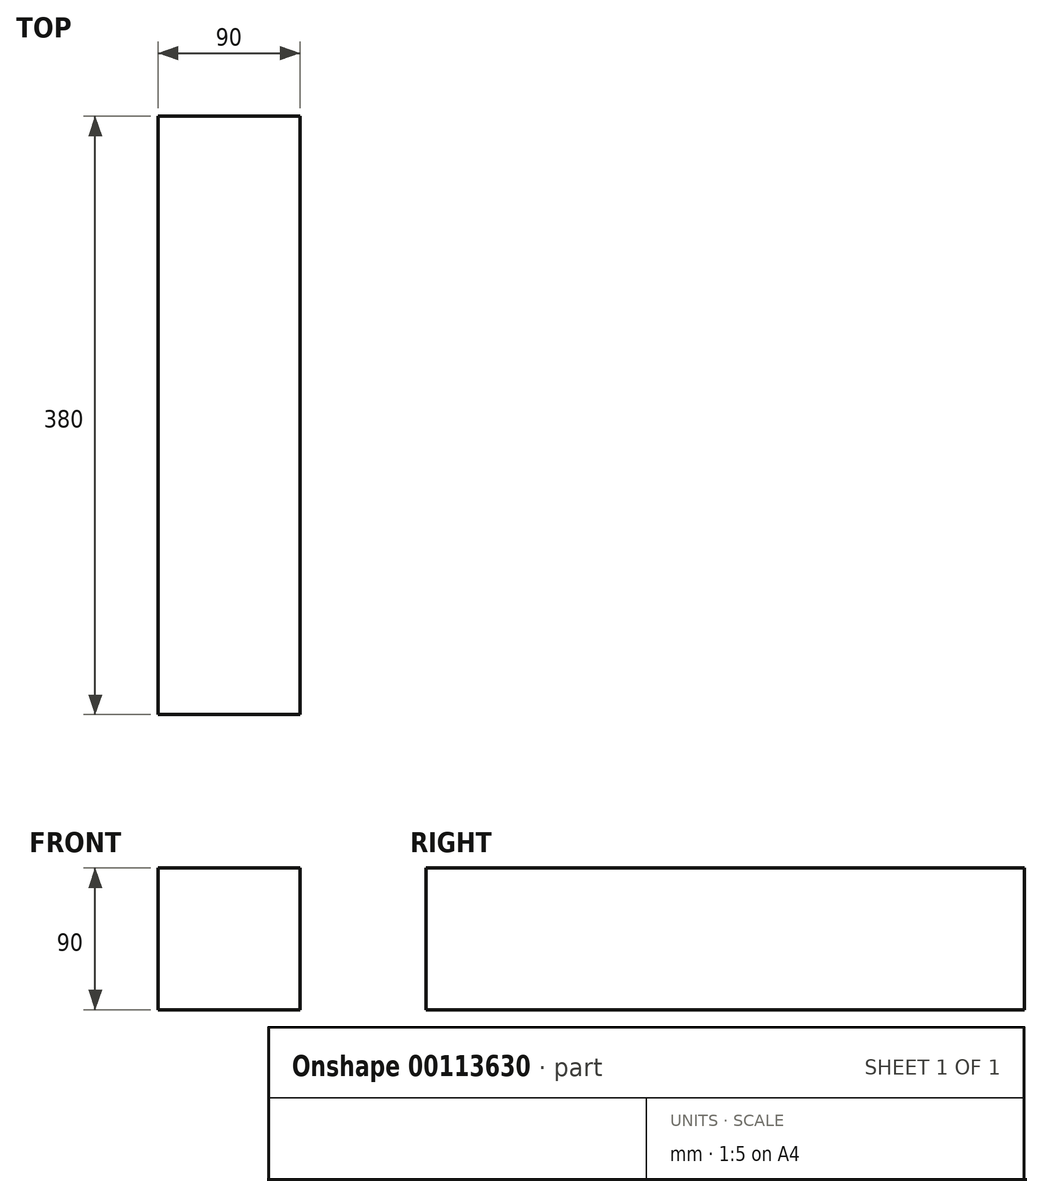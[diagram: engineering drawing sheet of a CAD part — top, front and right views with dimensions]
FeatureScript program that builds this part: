
annotation { "Feature Type Name" : "Feature", "Feature Type Description" : "" }
export const myFeature = defineFeature(function(context is Context, id is Id, definition is map)
    precondition{}
    {
        {
            var Q0;
            Q0=qCreatedBy(makeId("Front.planeOp"),FACE);
            var sketch = newSketch(context, id + "F0", { "sketchPlane" : qUnion([Q0])});
            skLineSegment(sketch, "E0.bottom", {"start": v(45, -45) * mm, "end": v(-45, -45) * mm});
            skLineSegment(sketch, "E0.top", {"start": v(45, 45) * mm, "end": v(-45, 45) * mm});
            skLineSegment(sketch, "E0.left", {"start": v(45, -45) * mm, "end": v(45, 45) * mm});
            skLineSegment(sketch, "E0.right", {"start": v(-45, -45) * mm, "end": v(-45, 45) * mm});
            skPoint(sketch, "E0.middle", {"position": v(0, 0) * mm});
            skSolve(sketch);
        }
        {
            var Q0;
            Q0=makeQuery(id+"F0.imprint","IMPRINT",FACE,{"disambiguationData":[TD([[makeQuery(id+"F0.imprint","IMPRINT",EDGE,{"derivedFrom":sQuery(id+"F0.wireOp",EDGE,"E0.bottom")}),-1.0]])]});
            extrude(context, id + "F1", {"entities" : qUnion([Q0]), "oppositeDirection" : true, "depth" : 380 * mm});
        }
    });
